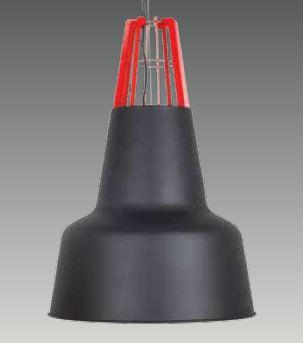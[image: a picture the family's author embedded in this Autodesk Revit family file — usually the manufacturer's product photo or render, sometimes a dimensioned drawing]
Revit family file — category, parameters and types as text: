
# Revit family: S 0500 DEL-9
name_source: partatom
category: Lighting Fixtures
revit_build: Autodesk Revit 2016 (Build: 20150714_1515(x64)
units: mm (PartAtom-declared; Revit-internal decimal feet)

## family parameters
Cut with Voids When Loaded = No
Host = Face
Light Source = Yes
Part Type = Normal
Room Calculation Point = No
Round Connector Dimension = Use Diameter
Shared = No

## types (2) — shared parameters
Color Filter = 16777215
Default Elevation = 1219 mm
Dimming Lamp Color Temperature Shift = <None>
Emit Shape Visible in Rendering = Yes
Emit from Circle Diameter = 490 mm  [stored 1.60761 ft]
Light Source Symbol Size = 610 mm
Manufacturer = ARLIGHT
Type Image = S 0500 DEL.JPG
Wattage Comments = 32

## type names (no varying parameters)
- SDEL.500.32.30
- SDEL.500.32.40

note: [stored X ft] marks values corroborated as IEEE doubles in the binary element streams (Revit-internal decimal feet)

## geometry (parser evidence)
native form markers: Sweep x3
no freeform markers — native parametric forms only
